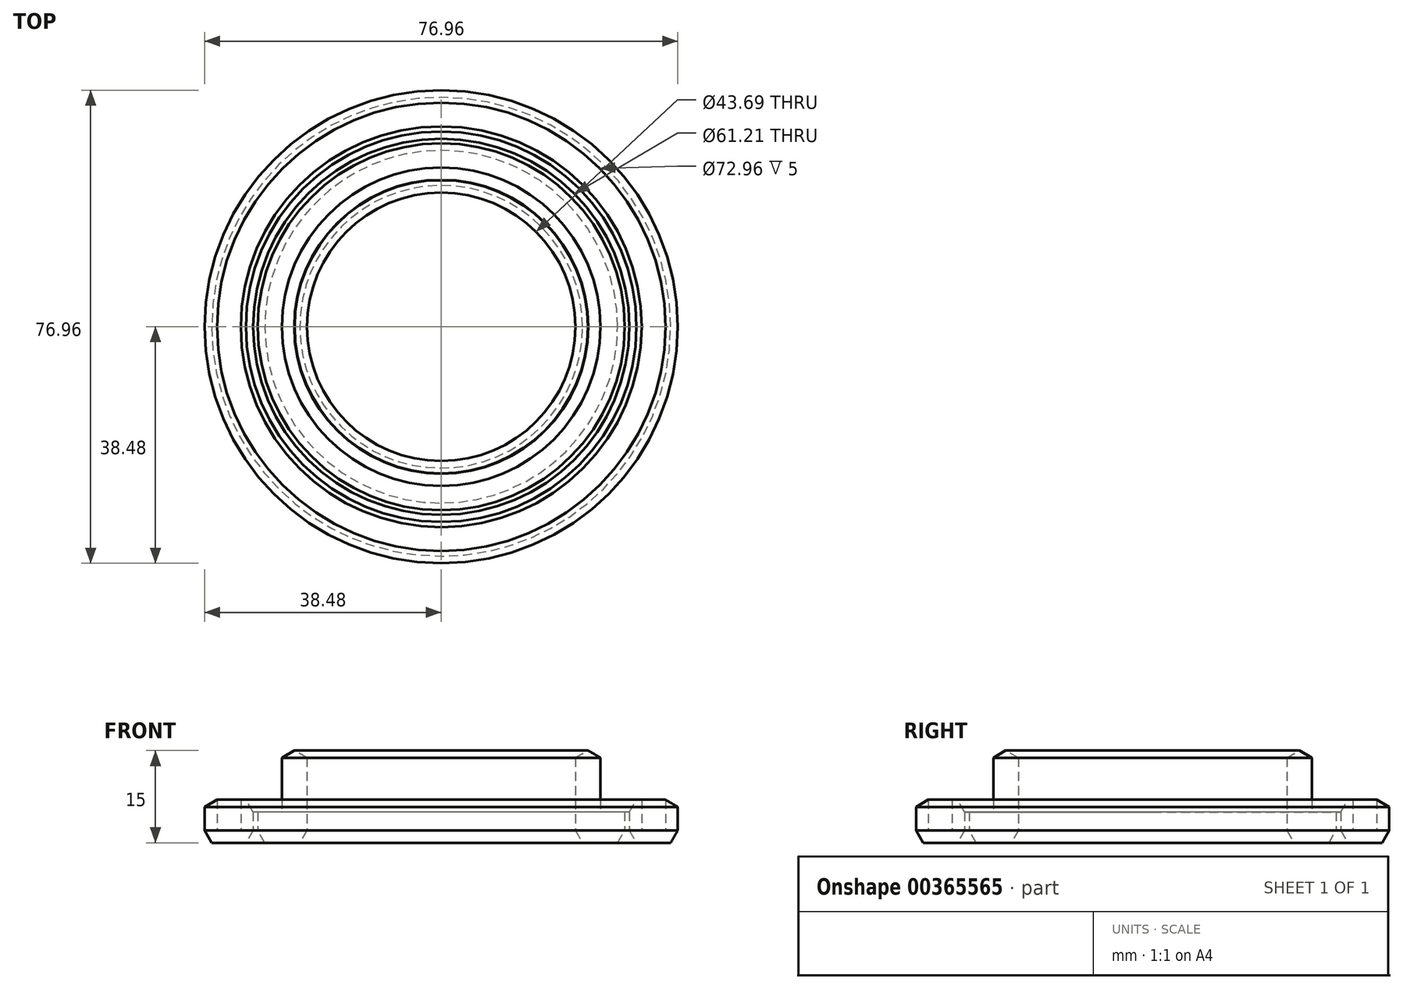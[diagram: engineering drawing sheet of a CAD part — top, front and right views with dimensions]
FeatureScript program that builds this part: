
annotation { "Feature Type Name" : "Feature", "Feature Type Description" : "" }
export const myFeature = defineFeature(function(context is Context, id is Id, definition is map)
    precondition{}
    {
        {
            var Q0;
            Q0=qCreatedBy(makeId("Top.planeOp"),FACE);
            var sketch = newSketch(context, id + "F0", { "sketchPlane" : qUnion([Q0])});
            skCircle(sketch, "E0", {"center": v(0, 0) * mm, "radius": 30.6 * mm});
            skCircle(sketch, "E1", {"center": v(0, 0) * mm, "radius": 38.48 * mm});
            skCircle(sketch, "E2", {"center": v(0, 0) * mm, "radius": 20.45 * mm, "construction": true});
            skCircle(sketch, "E3", {"center": v(0, 0) * mm, "radius": 44.45 * mm, "construction": true});
            skCircle(sketch, "E4", {"center": v(0, 0) * mm, "radius": 32.6 * mm});
            skCircle(sketch, "E5", {"center": v(0, 0) * mm, "radius": 36.48 * mm});
            skSolve(sketch);
        }
        {
            var Q0;
            Q0=makeQuery(id+"F0.imprint","IMPRINT",FACE,{"disambiguationData":[TD([[makeQuery(id+"F0.imprint","IMPRINT",EDGE,{"derivedFrom":sQuery(id+"F0.wireOp",EDGE,"E0")}),-1.0]])]});
            var Q1;
            Q1=makeQuery(id+"F0.imprint","IMPRINT",FACE,{"disambiguationData":[TD([[makeQuery(id+"F0.imprint","IMPRINT",EDGE,{"derivedFrom":sQuery(id+"F0.wireOp",EDGE,"E4")}),-1.0]])]});
            var Q2;
            Q2=makeQuery(id+"F0.imprint","IMPRINT",FACE,{"disambiguationData":[TD([[makeQuery(id+"F0.imprint","IMPRINT",EDGE,{"derivedFrom":sQuery(id+"F0.wireOp",EDGE,"E1")}),1.0]])]});
            extrude(context, id + "F1", {"entities" : qUnion([Q0, Q1, Q2]), "depth" : 2 * mm});
        }
        {
            var Q0;
            Q0=makeQuery(id+"F0.imprint","IMPRINT",FACE,{"disambiguationData":[TD([[makeQuery(id+"F0.imprint","IMPRINT",EDGE,{"derivedFrom":sQuery(id+"F0.wireOp",EDGE,"E1")}),1.0]])]});
            var Q1;
            Q1=makeQuery(id+"F0.imprint","IMPRINT",FACE,{"disambiguationData":[TD([[makeQuery(id+"F0.imprint","IMPRINT",EDGE,{"derivedFrom":sQuery(id+"F0.wireOp",EDGE,"E0")}),-1.0]])]});
            extrude(context, id + "F2", {"entities" : qUnion([Q0, Q1]), "operationType" : NewBodyOperationType.ADD, "depth" : 7 * mm});
        }
        {
            var Q0;
            Q0=qCreatedBy(makeId("Top.planeOp"),FACE);
            var sketch = newSketch(context, id + "F3", { "sketchPlane" : qUnion([Q0])});
            skCircle(sketch, "E6", {"center": v(0, 0) * mm, "radius": 29.85 * mm});
            skCircle(sketch, "E7", {"center": v(0, 0) * mm, "radius": 25.9 * mm});
            skCircle(sketch, "E8", {"center": v(0, 0) * mm, "radius": 21.84 * mm});
            skSolve(sketch);
        }
        {
            var Q0;
            Q0=makeQuery(id+"F3.imprint","IMPRINT",FACE,{"disambiguationData":[TD([[makeQuery(id+"F3.imprint","IMPRINT",EDGE,{"derivedFrom":sQuery(id+"F3.wireOp",EDGE,"E6")}),1.0]])]});
            var Q1;
            Q1=makeQuery(id+"F3.imprint","IMPRINT",FACE,{"disambiguationData":[TD([[makeQuery(id+"F3.imprint","IMPRINT",EDGE,{"derivedFrom":sQuery(id+"F3.wireOp",EDGE,"E7")}),1.0]])]});
            extrude(context, id + "F4", {"entities" : qUnion([Q0, Q1]), "depth" : 5 * mm});
        }
        {
            var Q0;
            Q0=makeQuery(id+"F3.imprint","IMPRINT",FACE,{"disambiguationData":[TD([[makeQuery(id+"F3.imprint","IMPRINT",EDGE,{"derivedFrom":sQuery(id+"F3.wireOp",EDGE,"E7")}),1.0]])]});
            extrude(context, id + "F5", {"entities" : qUnion([Q0]), "operationType" : NewBodyOperationType.ADD, "depth" : 15 * mm});
        }
        {
            var Q0;
            Q0=makeQuery(id+"F5.opExtrude","CAP_EDGE",EDGE,{"disambiguationData":[OSD([sQuery(id+"F3.wireOp",EDGE,"E7")])],"isStart":false});
            var Q1;
            Q1=makeQuery(id+"F5.opExtrude","CAP_EDGE",EDGE,{"disambiguationData":[OSD([sQuery(id+"F3.wireOp",EDGE,"E8")])],"isStart":false});
            var Q2;
            Q2=makeQuery(id+"F4.opExtrude","CAP_EDGE",EDGE,{"disambiguationData":[OSD([sQuery(id+"F3.wireOp",EDGE,"E8")])],"isStart":true});
            chamfer(context, id + "F6", {"entities" : qUnion([Q0, Q1, Q2]), "chamferType" : ChamferType.OFFSET_ANGLE, "width" : 2 * mm, "oppositeDirection" : true, "angle" : 30 * degree, "tangentPropagation" : true});
        }
        {
            var Q0;
            Q0=makeQuery(id+"F4.opExtrude","CAP_EDGE",EDGE,{"disambiguationData":[OSD([sQuery(id+"F3.wireOp",EDGE,"E6")])],"isStart":true});
            chamfer(context, id + "F7", {"entities" : qUnion([Q0]), "chamferType" : ChamferType.OFFSET_ANGLE, "width" : 2 * mm, "oppositeDirection" : false, "angle" : 30 * degree, "tangentPropagation" : true});
        }
        {
            var Q0;
            Q0=makeQuery(id+"F2.opExtrude","CAP_EDGE",EDGE,{"disambiguationData":[OSD([sQuery(id+"F0.wireOp",EDGE,"E1")])],"isStart":false});
            var Q1;
            Q1=makeQuery(id+"F1.opExtrude","CAP_EDGE",EDGE,{"disambiguationData":[OSD([sQuery(id+"F0.wireOp",EDGE,"E1")])],"isStart":true});
            chamfer(context, id + "F8", {"entities" : qUnion([Q0, Q1]), "chamferType" : ChamferType.OFFSET_ANGLE, "width" : 2 * mm, "oppositeDirection" : true, "angle" : 30 * degree, "tangentPropagation" : true});
        }
        {
            var Q0;
            Q0=makeQuery(id+"F2.opExtrude","CAP_EDGE",EDGE,{"disambiguationData":[OSD([sQuery(id+"F0.wireOp",EDGE,"E0")])],"isStart":false});
            var Q1;
            Q1=makeQuery(id+"F1.opExtrude","CAP_EDGE",EDGE,{"disambiguationData":[OSD([sQuery(id+"F0.wireOp",EDGE,"E0")])],"isStart":true});
            chamfer(context, id + "F9", {"entities" : qUnion([Q0, Q1]), "chamferType" : ChamferType.OFFSET_ANGLE, "width" : 2 * mm, "oppositeDirection" : false, "angle" : 30 * degree, "tangentPropagation" : true});
        }
    });
